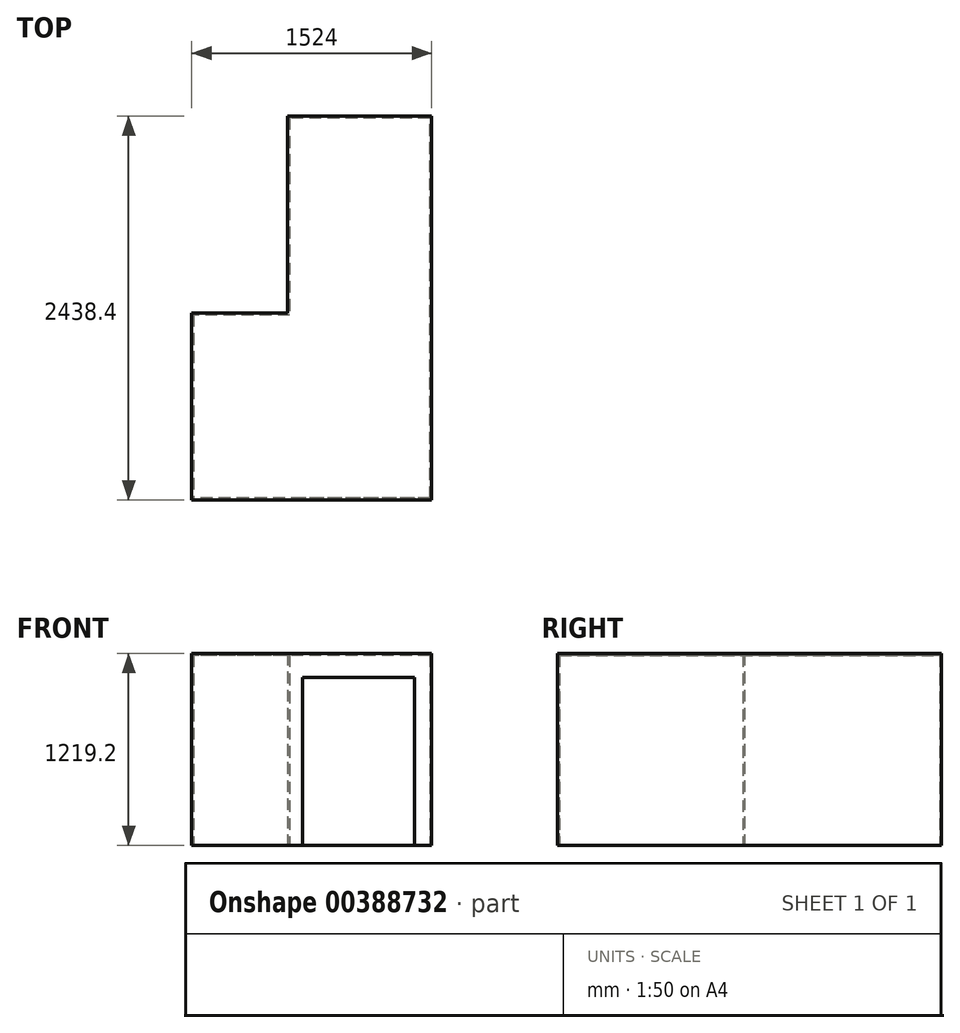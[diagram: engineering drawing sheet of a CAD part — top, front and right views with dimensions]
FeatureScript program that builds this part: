
annotation { "Feature Type Name" : "Feature", "Feature Type Description" : "" }
export const myFeature = defineFeature(function(context is Context, id is Id, definition is map)
    precondition{}
    {
        {
            var Q0;
            Q0=qCreatedBy(makeId("Top.planeOp"),FACE);
            var sketch = newSketch(context, id + "F0", { "sketchPlane" : qUnion([Q0])});
            skLineSegment(sketch, "E0.bottom", {"start": v(1828.8, 1219.2) * mm, "end": v(-1828.8, 1219.2) * mm});
            skLineSegment(sketch, "E0.top", {"start": v(1828.8, -1219.2) * mm, "end": v(-1828.8, -1219.2) * mm});
            skLineSegment(sketch, "E0.left", {"start": v(1828.8, 1219.2) * mm, "end": v(1828.8, -1219.2) * mm});
            skLineSegment(sketch, "E0.right", {"start": v(-1828.8, 1219.2) * mm, "end": v(-1828.8, -1219.2) * mm});
            skPoint(sketch, "E0.middle", {"position": v(0, 0) * mm});
            skLineSegment(sketch, "E1", {"start": v(1816.9, -1207.3) * mm, "end": v(1828.8, -1207.3) * mm});
            skLineSegment(sketch, "E2", {"start": v(-1816.9, 0) * mm, "end": v(1828.8, 0) * mm, "construction": true});
            skLineSegment(sketch, "E3", {"start": v(-914.4, 1219.2) * mm, "end": v(-914.4, -1219.2) * mm, "construction": true});
            skLineSegment(sketch, "E4.1.0.0", {"start": v(0, 1219.2) * mm, "end": v(0, -1219.2) * mm, "construction": true});
            skLineSegment(sketch, "E4.2.0.0", {"start": v(914.4, 1219.2) * mm, "end": v(914.4, -1219.2) * mm, "construction": true});
            skLineSegment(sketch, "E4.direction1", {"start": v(-914.4, -1219.2) * mm, "end": v(0, -1219.2) * mm, "construction": true});
            skLineSegment(sketch, "E5.bottom", {"start": v(6486.53, -1219.2) * mm, "end": v(4048.13, -1219.2) * mm});
            skLineSegment(sketch, "E5.top", {"start": v(6486.53, 1219.2) * mm, "end": v(4048.13, 1219.2) * mm});
            skLineSegment(sketch, "E5.left", {"start": v(6486.53, -1219.2) * mm, "end": v(6486.53, 1219.2) * mm});
            skLineSegment(sketch, "E5.right", {"start": v(4048.13, -1219.2) * mm, "end": v(4048.13, 1219.2) * mm});
            skPoint(sketch, "E5.middle", {"position": v(5267.33, 0) * mm});
            skLineSegment(sketch, "E6", {"start": v(5572.13, 1219.2) * mm, "end": v(5572.13, -31.75) * mm});
            skLineSegment(sketch, "E7", {"start": v(5572.13, -31.75) * mm, "end": v(4962.53, -31.75) * mm});
            skLineSegment(sketch, "E8", {"start": v(4962.53, -31.75) * mm, "end": v(4962.53, -1219.2) * mm});
            skSolve(sketch);
        }
        {
            var Q0;
            {var subQ1=sQuery(id+"F0.wireOp",EDGE,"E5.left");Q0=makeQuery(id+"F0.imprint","IMPRINT",FACE,{"disambiguationData":[TD([[makeQuery(id+"F0.imprint","IMPRINT",EDGE,{"derivedFrom":subQ1}),1.0]])]});}
            extrude(context, id + "F1", {"entities" : qUnion([Q0]), "depth" : 1219.2 * mm});
        }
        {
            var Q0;
            Q0=makeQuery(id+"F1.opExtrude","CAP_FACE",FACE,{"disambiguationData":[OSD([sQuery(id+"F0.wireOp",EDGE,"E5.bottom"),sQuery(id+"F0.wireOp",EDGE,"E5.top"),sQuery(id+"F0.wireOp",EDGE,"E5.left"),sQuery(id+"F0.wireOp",EDGE,"E6"),sQuery(id+"F0.wireOp",EDGE,"E7"),sQuery(id+"F0.wireOp",EDGE,"E8")])],"isStart":true});
            var Q1;
            Q1=makeQuery(id+"F1.opExtrude","SWEPT_BODY",BODY,{"disambiguationData":[OSD([sQuery(id+"F0.wireOp",EDGE,"E5.bottom"),sQuery(id+"F0.wireOp",EDGE,"E5.top"),sQuery(id+"F0.wireOp",EDGE,"E5.left"),sQuery(id+"F0.wireOp",EDGE,"E6"),sQuery(id+"F0.wireOp",EDGE,"E7"),sQuery(id+"F0.wireOp",EDGE,"E8")])]});
            shell(context, id + "F2", {"entities" : qUnion([Q0]), "parts" : qUnion([Q1]), "thickness" : 11.9 * mm});
        }
        {
            var Q0;
            Q0=makeQuery(id+"F1.opExtrude","SWEPT_FACE",FACE,{"disambiguationData":[OSD([sQuery(id+"F0.wireOp",EDGE,"E5.bottom")])]});
            var sketch = newSketch(context, id + "F3", { "sketchPlane" : qUnion([Q0])});
            skLineSegment(sketch, "E9.bottom", {"start": v(6378.1, 0) * mm, "end": v(5666.9, 0) * mm});
            skLineSegment(sketch, "E9.top", {"start": v(6378.1, 1066.8) * mm, "end": v(5666.9, 1066.8) * mm});
            skLineSegment(sketch, "E9.left", {"start": v(6378.1, 0) * mm, "end": v(6378.1, 1066.8) * mm});
            skLineSegment(sketch, "E9.right", {"start": v(5666.9, 0) * mm, "end": v(5666.9, 1066.8) * mm});
            skSolve(sketch);
        }
        {
            var Q0;
            Q0=makeQuery(id+"F3.imprint","IMPRINT",FACE,{"disambiguationData":[TD([[makeQuery(id+"F3.imprint","IMPRINT",EDGE,{"derivedFrom":sQuery(id+"F3.wireOp",EDGE,"E9.bottom")}),-1.0]])]});
            extrude(context, id + "F4", {"entities" : qUnion([Q0]), "operationType" : NewBodyOperationType.REMOVE, "oppositeDirection" : true, "depth" : 25.4 * mm});
        }
    });
